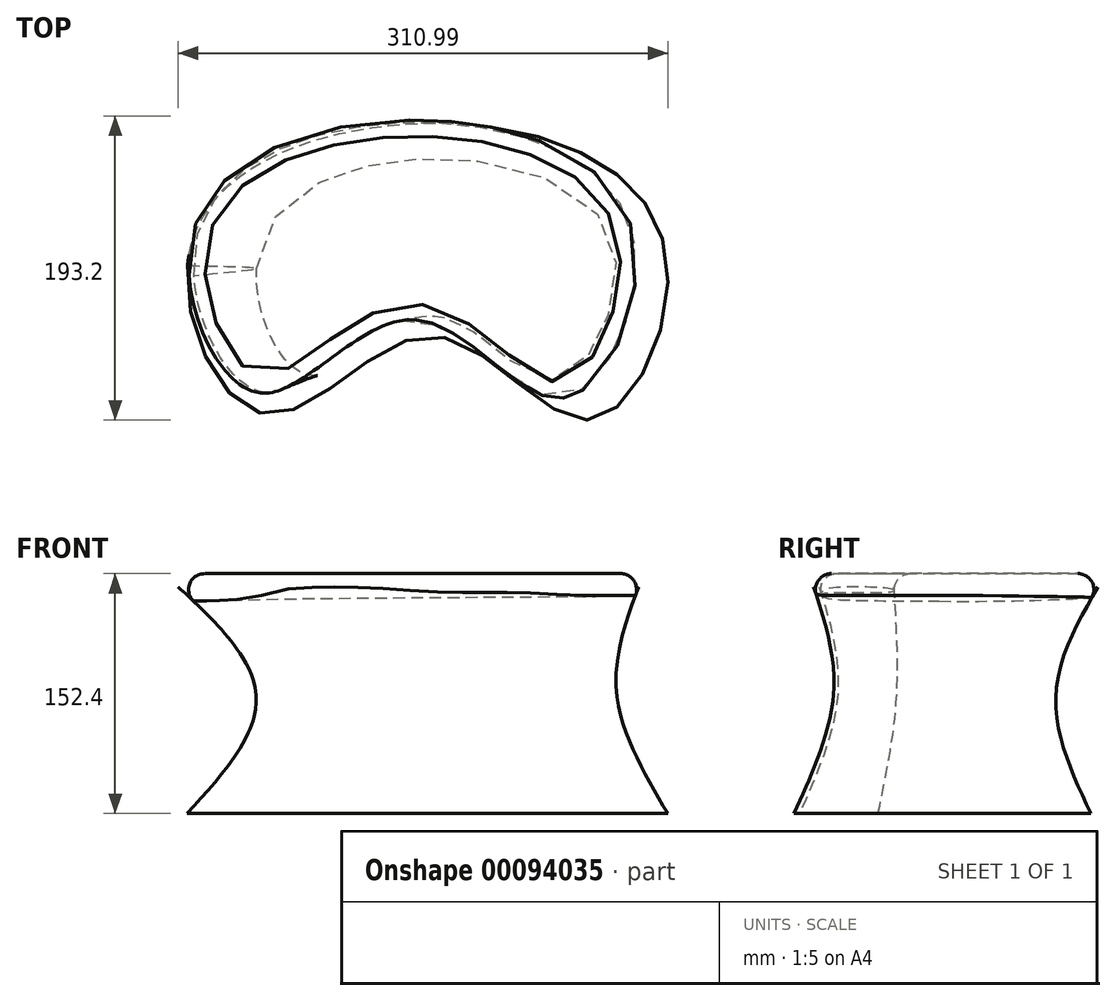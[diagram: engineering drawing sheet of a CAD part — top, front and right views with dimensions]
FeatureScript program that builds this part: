
annotation { "Feature Type Name" : "Feature", "Feature Type Description" : "" }
export const myFeature = defineFeature(function(context is Context, id is Id, definition is map)
    precondition{}
    {
        {
            var Q0;
            Q0=qCreatedBy(makeId("Top.planeOp"),FACE);
            var sketch = newSketch(context, id + "F0", { "sketchPlane" : qUnion([Q0])});
            skPoint(sketch, "E0", {"position": v(-155.33, 0) * mm});
            skPoint(sketch, "E1", {"position": v(149.47, 0) * mm});
            skFitSpline(sketch, "E2", {"points": [v(-155.33, 0) * mm, v(-80.56, 77.68) * mm, v(78.98, 78.17) * mm, v(149.47, 0) * mm, v(99.17, -98.09) * mm, v(0, -44.6) * mm, v(-103.88, -94.5) * mm, v(-155.33, 0) * mm]});
            skSolve(sketch);
        }
        {
            var Q0;
            Q0=qCreatedBy(makeId("Top.planeOp"),FACE);
            cPlane(context, id + "F1", {"entities" : qUnion([Q0]), "cplaneType" : CPlaneType.OFFSET, "offset" : 152.4 * mm, "width" : 152.4 * mm, "height" : 152.4 * mm});
        }
        {
            var Q0;
            Q0=qCreatedBy(id+"F1.planeOp",FACE);
            var sketch = newSketch(context, id + "F2", { "sketchPlane" : qUnion([Q0])});
            skPoint(sketch, "E3", {"position": v(-170.4, 9.64) * mm});
            skPoint(sketch, "E4", {"position": v(134.4, 9.64) * mm});
            skFitSpline(sketch, "E5", {"points": [v(-170.4, 9.64) * mm, v(-95.63, 87.32) * mm, v(63.91, 87.81) * mm, v(134.4, 9.64) * mm, v(84.1, -88.44) * mm, v(-15.07, -34.95) * mm, v(-118.95, -84.86) * mm, v(-170.4, 9.64) * mm]});
            skSolve(sketch);
        }
        {
            var Q0;
            Q0=qCreatedBy(makeId("Top.planeOp"),FACE);
            cPlane(context, id + "F3", {"entities" : qUnion([Q0]), "cplaneType" : CPlaneType.OFFSET, "offset" : 76.2 * mm, "width" : 152.4 * mm, "height" : 152.4 * mm});
        }
        {
            var Q0;
            Q0=qCreatedBy(id+"F3.planeOp",FACE);
            var sketch = newSketch(context, id + "F4", { "sketchPlane" : qUnion([Q0])});
            skPoint(sketch, "E6", {"position": v(-111.6, 0.73) * mm});
            skPoint(sketch, "E7", {"position": v(117, 3.04) * mm});
            skFitSpline(sketch, "E8", {"points": [v(-111.6, 0.73) * mm, v(-57.83, 58.98) * mm, v(61.83, 59.35) * mm, v(117, 3.04) * mm, v(76.97, -72.84) * mm, v(2.59, -32.72) * mm, v(-75.32, -70.15) * mm, v(-111.6, 0.73) * mm]});
            skSolve(sketch);
        }
        {
            var Q0;
            Q0=makeQuery(id+"F0.imprint","IMPRINT",FACE,{"disambiguationData":[TD([[makeQuery(id+"F0.imprint","IMPRINT",EDGE,{"derivedFrom":sQuery(id+"F0.wireOp",EDGE,"E2")}),-1.0]])]});
            var Q1;
            Q1=makeQuery(id+"F4.imprint","IMPRINT",FACE,{"disambiguationData":[TD([[makeQuery(id+"F4.imprint","IMPRINT",EDGE,{"derivedFrom":sQuery(id+"F4.wireOp",EDGE,"E8")}),-1.0]])]});
            var Q2;
            Q2=makeQuery(id+"F2.imprint","IMPRINT",FACE,{"disambiguationData":[TD([[makeQuery(id+"F2.imprint","IMPRINT",EDGE,{"derivedFrom":sQuery(id+"F2.wireOp",EDGE,"E5")}),-1.0]])]});
            loft(context, id + "F5", {"sheetProfilesArray" : [{ "sheetProfileEntities" : qUnion([Q0]) }, { "sheetProfileEntities" : qUnion([Q1]) }, { "sheetProfileEntities" : qUnion([Q2]) }]});
        }
        {
            var Q0;
            Q0=makeQuery(id+"F5.opLoft","MID_CAP_EDGE",EDGE,{"disambiguationData":[OSD([sQuery(id+"F0.wireOp",EDGE,"E2"),sQuery(id+"F2.wireOp",EDGE,"E5")])],"capPos":2.0});
            fillet(context, id + "F6", {"entities" : qUnion([Q0]), "radius" : 10.16 * mm, "tangentPropagation" : true, "allowEdgeOverflow" : false});
        }
    });
